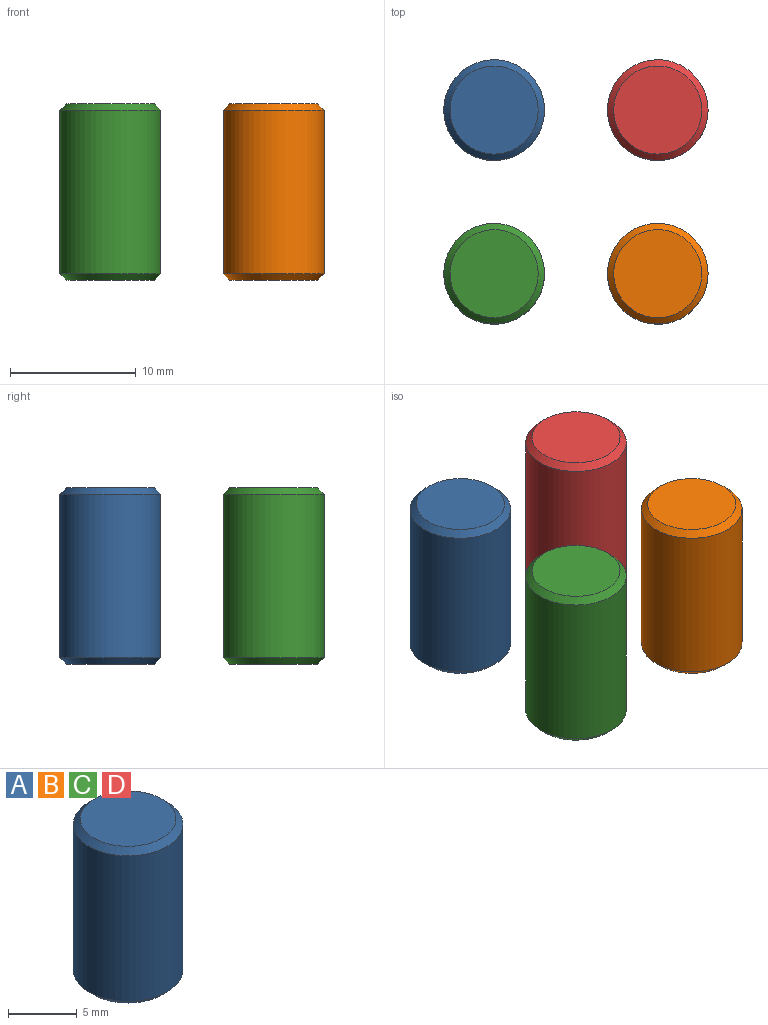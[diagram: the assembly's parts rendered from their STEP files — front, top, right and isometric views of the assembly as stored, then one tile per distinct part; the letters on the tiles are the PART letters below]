
ASSEMBLY  parts=4 mates=3
PART A: 5 faces, bbox 8x8x14 mm
  f0: cylinder r=4mm len=13mm, axis (0,0,-1), area 326.7mm2, adj f3,f4
  f1: plane 7x7mm, normal (0,0,1), area 38.5mm2, adj f3
  f2: plane 7x7mm, normal (0,0,-1), area 38.5mm2, adj f4
  f3: cone r=3.5mm half-angle=45deg, axis (0,0,-1), area 16.7mm2, adj f0,f1
  f4: cone r=4mm half-angle=45deg, axis (0,0,1), area 16.7mm2, adj f0,f2
PART B: same geometry as A
PART C: same geometry as A
PART D: same geometry as A
PLACE A at identity fixed
PLACE B t=(13,-13,0)mm
PLACE C t=(0,-13,0)mm
PLACE D t=(13,0,0)mm
MATE fastened B.f0 <-> A.f2  axis (0,0,-1) through (13,-13,0)mm
MATE fastened C.f0 <-> A.f2  axis (0,0,-1) through (0,-13,0)mm
MATE fastened D.f0 <-> A.f2  axis (0,0,-1) through (13,0,0)mm
